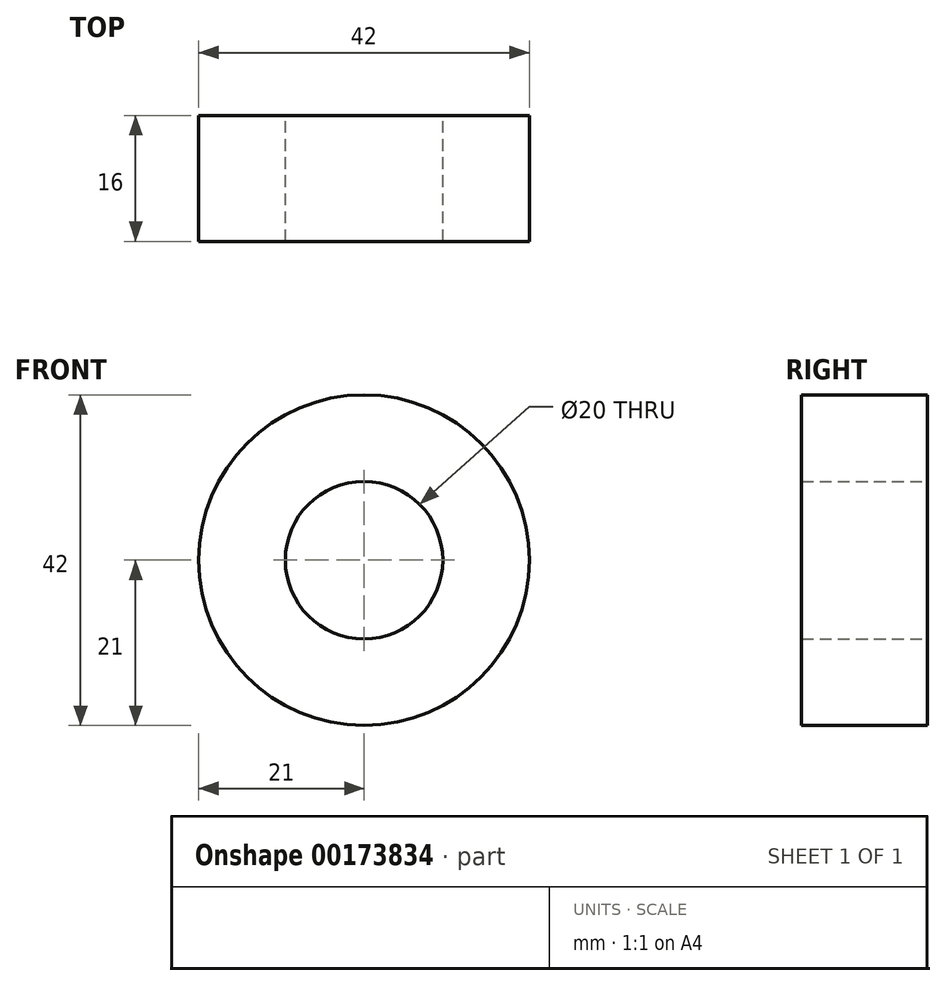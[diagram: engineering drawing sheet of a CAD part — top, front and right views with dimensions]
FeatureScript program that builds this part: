
annotation { "Feature Type Name" : "Feature", "Feature Type Description" : "" }
export const myFeature = defineFeature(function(context is Context, id is Id, definition is map)
    precondition{}
    {
        {
            var Q0;
            Q0=qCreatedBy(makeId("Front.planeOp"),FACE);
            var sketch = newSketch(context, id + "F0", { "sketchPlane" : qUnion([Q0])});
            skCircle(sketch, "E0", {"center": v(0, 0) * mm, "radius": 10 * mm});
            skCircle(sketch, "E1", {"center": v(0, 0) * mm, "radius": 21 * mm});
            skSolve(sketch);
        }
        {
            var Q0;
            Q0 = qSketchRegion(id + "F0", true);
            extrude(context, id + "F1", {"entities" : qUnion([Q0]), "depth" : 16 * mm});
        }
    });
